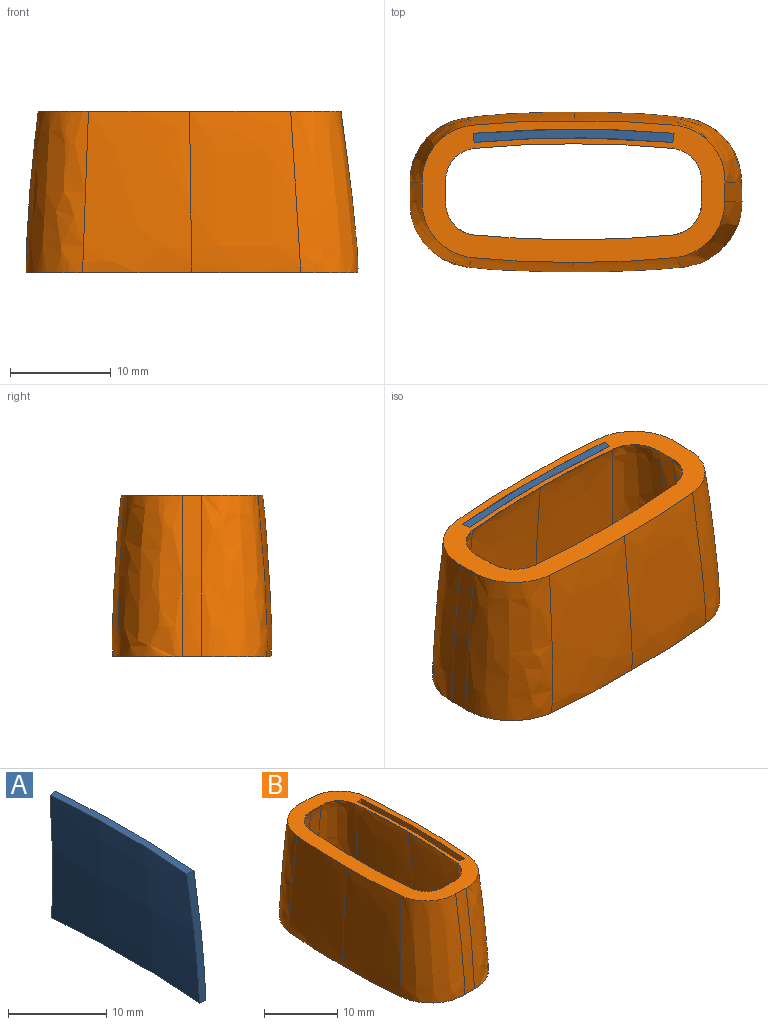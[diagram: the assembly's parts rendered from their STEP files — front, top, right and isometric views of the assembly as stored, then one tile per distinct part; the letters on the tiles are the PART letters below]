
ASSEMBLY  parts=2 mates=1
PART A: 6 faces, bbox 2.3x21.5x16 mm
  f0: bspline ~21.3x16mm, area 329.1mm2, adj f1,f3,f4,f5
  f1: bspline ~16x1.66mm, area 13.9mm2, adj f0,f2,f4,f5
  f2: bspline ~21.5x16mm, area 332.5mm2, adj f1,f3,f4,f5
  f3: bspline ~16x1.66mm, area 14mm2, adj f0,f2,f4,f5
  f4: plane 19.93x1.31mm, normal (0,0,1), area 17.4mm2, adj f0,f1,f2,f3
  f5: plane 21.5x1.32mm, normal (0,0,-1), area 18.5mm2, adj f0,f1,f2,f3
PART B: 26 faces, bbox 20.1x37.3x20.4 mm
  f0: plane 33.32x16.14mm, normal (0,0,-1), area 156.1mm2, adj f2,f3,f4,f5,f6,f7,f8,f9
  f1: plane 30.24x14.21mm, normal (0,0,1), area 142.3mm2, adj f2,f3,f4,f5,f6,f7,f8,f9
  f2: offset ~20.4x9.06mm, area 143.9mm2, adj f0,f1,f3,f9
  f3: offset ~20.4x15mm, area 167.6mm2, adj f0,f1,f2,f4
  f4: offset ~20.4x15.21mm, area 167.6mm2, adj f0,f1,f3,f5
  f5: offset ~20.4x9.58mm, area 144.1mm2, adj f0,f1,f4,f6
  f6: offset ~20.4x6.67mm, area 31.2mm2, adj f0,f1,f5,f7
  f7: offset ~20.4x9.31mm, area 143.9mm2, adj f0,f1,f6,f11
  f8: offset ~20.4x8.88mm, area 143.8mm2, adj f0,f1,f9,f10
  f9: offset ~20.4x6.4mm, area 31mm2, adj f0,f1,f2,f8
  f10: offset ~20.4x15mm, area 167.7mm2, adj f0,f1,f8,f11
  f11: offset ~20.4x15.21mm, area 167.7mm2, adj f0,f1,f7,f10
  f12: bspline ~16x10.81mm, area 164.2mm2, adj f0,f1,f13,f16
  f13: bspline ~16x10.6mm, area 164.2mm2, adj f0,f1,f12,f15
  f14: bspline ~16x2mm, area 32.2mm2, adj f0,f1,f15,f21
  f15: bspline ~16x4.48mm, area 92.6mm2, adj f0,f1,f13,f14
  f16: bspline ~16x4.91mm, area 92.7mm2, adj f0,f1,f12,f17
  f17: bspline ~16x2.27mm, area 32.3mm2, adj f0,f1,f16,f18
  f18: bspline ~16x5.18mm, area 92.7mm2, adj f0,f1,f17,f19
  f19: bspline ~16x10.81mm, area 164.3mm2, adj f0,f1,f18,f20
  f20: bspline ~16x10.6mm, area 164.2mm2, adj f0,f1,f19,f21
  f21: bspline ~16x4.66mm, area 92.6mm2, adj f0,f1,f14,f20
  f22: bspline ~21.3x16mm, area 329.1mm2, adj f0,f1,f23,f25
  f23: bspline ~16x1.66mm, area 13.9mm2, adj f0,f1,f22,f24
  f24: bspline ~21.5x16mm, area 332.5mm2, adj f0,f1,f23,f25
  f25: bspline ~16x1.66mm, area 14mm2, adj f0,f1,f22,f24
PLACE A rot(axis=(0,0,1),90deg) t=(10.15,0.01,0)mm
PLACE B rot(axis=(0,0,1),90deg) t=(10.15,0.01,0)mm
MATE fastened B.f1 <-> A.f4  axis (0,0,1) through (20.01,4.9,16)mm
